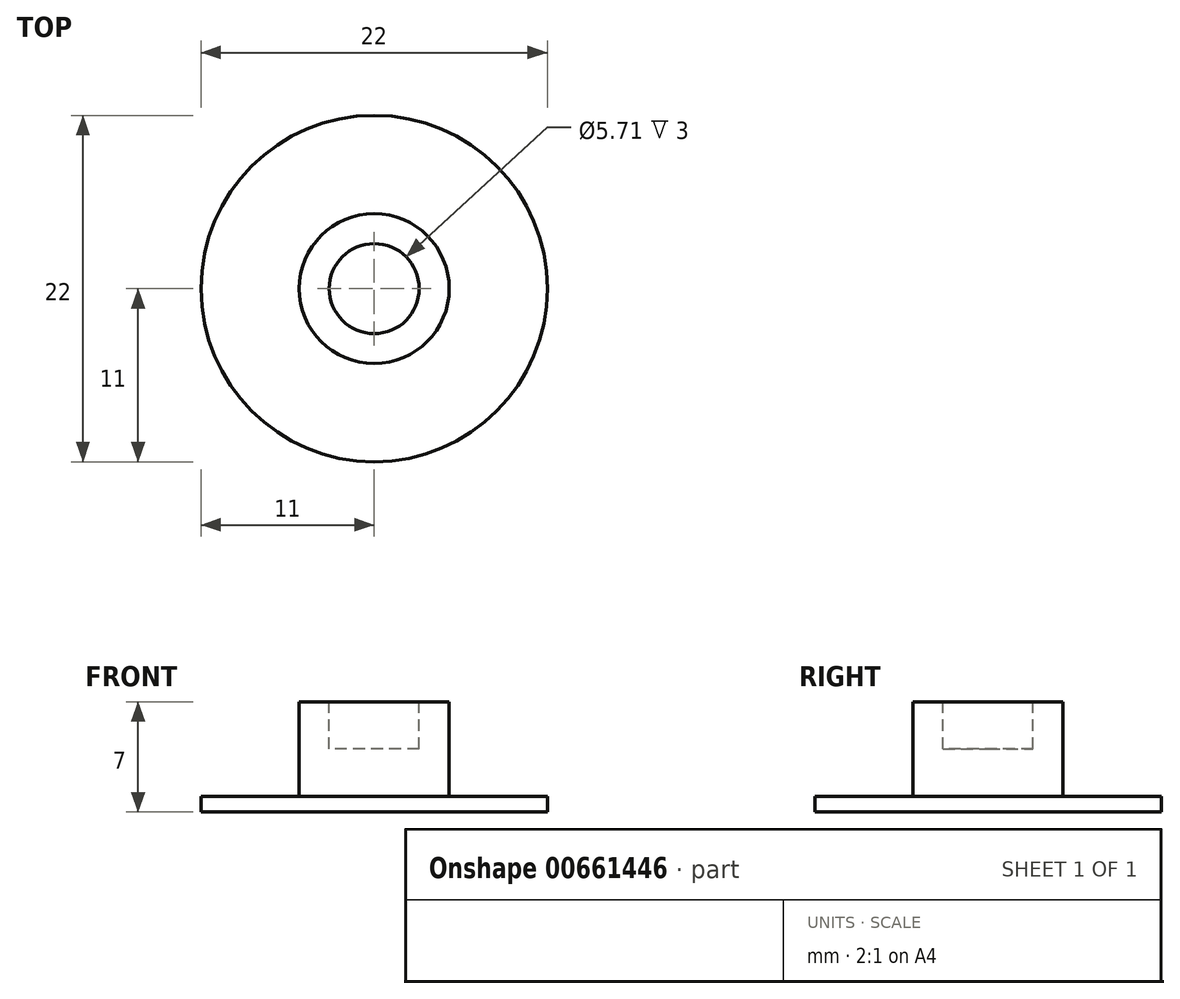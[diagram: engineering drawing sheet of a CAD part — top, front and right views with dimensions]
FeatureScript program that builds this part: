
annotation { "Feature Type Name" : "Feature", "Feature Type Description" : "" }
export const myFeature = defineFeature(function(context is Context, id is Id, definition is map)
    precondition{}
    {
        {
            var Q0;
            Q0=qCreatedBy(makeId("Top.planeOp"),FACE);
            var sketch = newSketch(context, id + "F0", { "sketchPlane" : qUnion([Q0])});
            skCircle(sketch, "E0", {"center": v(0, 0) * mm, "radius": 4.76 * mm});
            skCircle(sketch, "E1", {"center": v(0, 0) * mm, "radius": 2.61 * mm});
            skCircle(sketch, "E2", {"center": v(0, 0) * mm, "radius": 11 * mm});
            skSolve(sketch);
        }
        {
            var Q0;
            Q0=makeQuery(id+"F0.imprint","IMPRINT",FACE,{"disambiguationData":[TD([[makeQuery(id+"F0.imprint","IMPRINT",EDGE,{"derivedFrom":sQuery(id+"F0.wireOp",EDGE,"E0")}),1.0]])]});
            var Q1;
            Q1=makeQuery(id+"F0.imprint","IMPRINT",FACE,{"disambiguationData":[TD([[makeQuery(id+"F0.imprint","IMPRINT",EDGE,{"derivedFrom":sQuery(id+"F0.wireOp",EDGE,"E1")}),1.0]])]});
            extrude(context, id + "F1", {"entities" : qUnion([Q0, Q1]), "depth" : 7 * mm, "offsetDistance" : 25.4 * mm});
        }
        {
            var Q0;
            Q0=makeQuery(id+"F0.imprint","IMPRINT",FACE,{"disambiguationData":[TD([[makeQuery(id+"F0.imprint","IMPRINT",EDGE,{"derivedFrom":sQuery(id+"F0.wireOp",EDGE,"E0")}),-1.0]])]});
            var Q1;
            Q1=sQuery(id+"F0.wireOp",EDGE,"E1");
            extrude(context, id + "F2", {"entities" : qUnion([Q0]), "operationType" : NewBodyOperationType.ADD, "surfaceEntities" : qUnion([Q1]), "depth" : 1 * mm, "offsetDistance" : 25.4 * mm});
        }
        {
            var Q0;
            Q0=makeQuery(id+"F1.opExtrude","CAP_FACE",FACE,{"disambiguationData":[OSD([sQuery(id+"F0.wireOp",EDGE,"E0")])],"isStart":false});
            var sketch = newSketch(context, id + "F3", { "sketchPlane" : qUnion([Q0])});
            skCircle(sketch, "E3", {"center": v(0, 0) * mm, "radius": 2.86 * mm});
            skSolve(sketch);
        }
        {
            var Q0;
            Q0=makeQuery(id+"F3.imprint","IMPRINT",FACE,{"disambiguationData":[TD([[makeQuery(id+"F3.imprint","IMPRINT",EDGE,{"derivedFrom":sQuery(id+"F3.wireOp",EDGE,"E3")}),1.0]])]});
            var Q1;
            Q1=sQuery(id+"F3.wireOp",EDGE,"E3");
            extrude(context, id + "F4", {"entities" : qUnion([Q0]), "operationType" : NewBodyOperationType.REMOVE, "surfaceEntities" : qUnion([Q1]), "oppositeDirection" : true, "depth" : 3 * mm, "offsetDistance" : 25.4 * mm});
        }
    });
